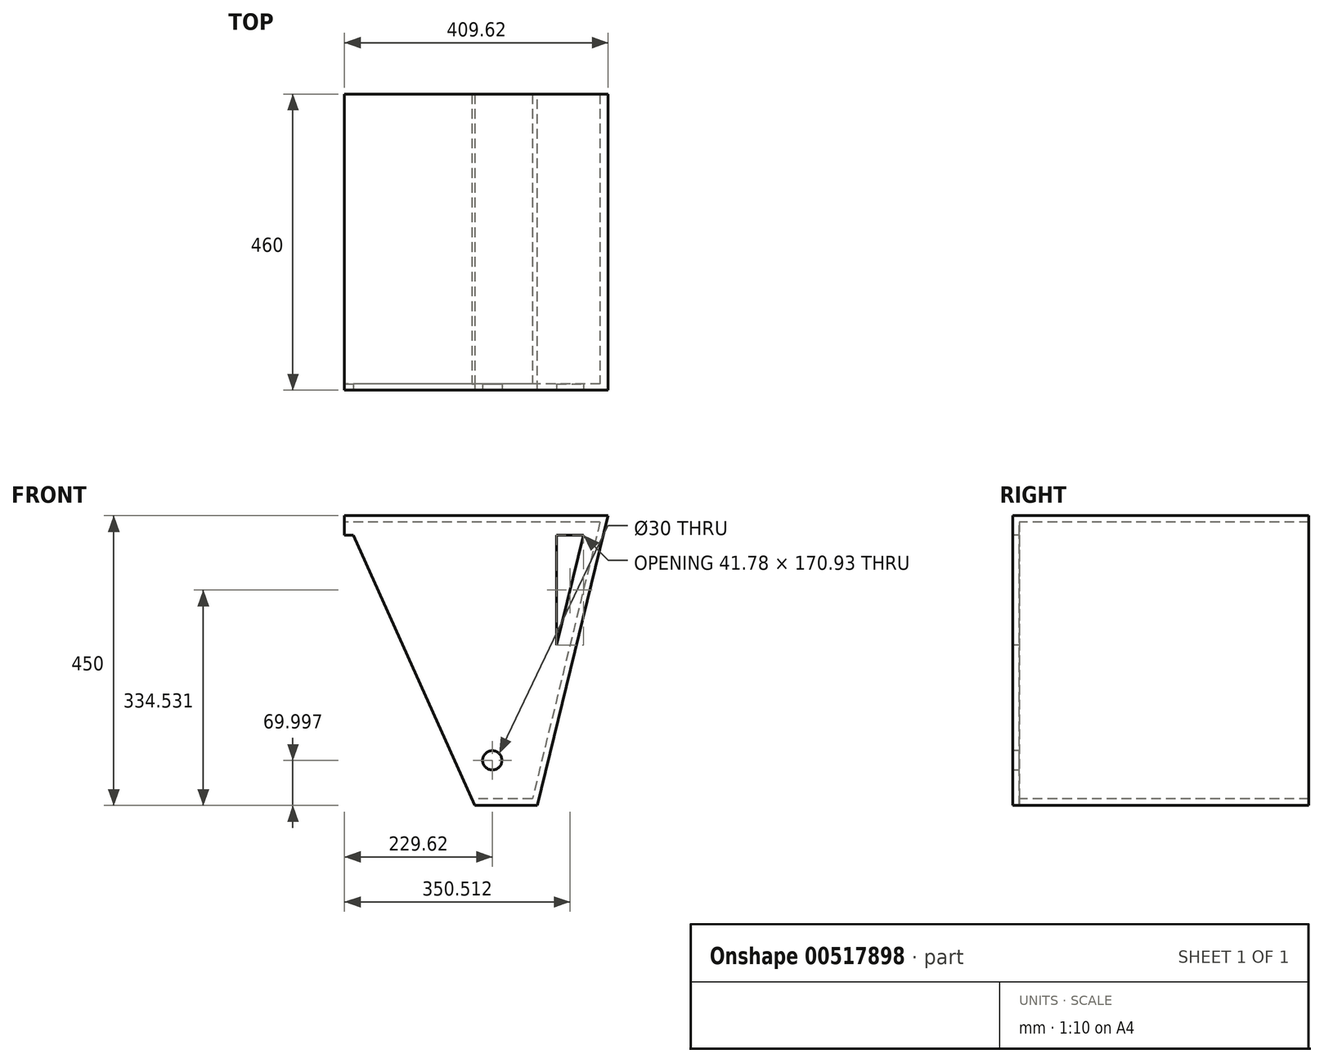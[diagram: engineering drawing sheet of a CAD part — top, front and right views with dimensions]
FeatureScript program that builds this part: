
annotation { "Feature Type Name" : "Feature", "Feature Type Description" : "" }
export const myFeature = defineFeature(function(context is Context, id is Id, definition is map)
    precondition{}
    {
        {
            var Q0;
            Q0=qCreatedBy(makeId("Front.planeOp"),FACE);
            var sketch = newSketch(context, id + "F0", { "sketchPlane" : qUnion([Q0])});
            skLineSegment(sketch, "E0.1", {"start": v(-436.34, 213.95) * mm, "end": v(-436.34, -176.05) * mm});
            skLineSegment(sketch, "E0.3", {"start": v(103.66, 213.95) * mm, "end": v(103.66, -176.05) * mm});
            skLineSegment(sketch, "E1", {"start": v(-465.58, -206.05) * mm, "end": v(133.66, -206.05) * mm});
            skLineSegment(sketch, "E2", {"start": v(-436.34, -176.05) * mm, "end": v(103.66, -176.05) * mm});
            skLineSegment(sketch, "E3", {"start": v(-436.34, 213.95) * mm, "end": v(103.66, 213.95) * mm});
            skLineSegment(sketch, "E4", {"start": v(-465.58, 243.95) * mm, "end": v(133.66, 243.95) * mm});
            skLineSegment(sketch, "E5", {"start": v(-465.58, 243.95) * mm, "end": v(-575.58, 243.95) * mm});
            skLineSegment(sketch, "E6", {"start": v(133.66, 243.95) * mm, "end": v(243.66, 243.95) * mm});
            skLineSegment(sketch, "E7", {"start": v(-575.58, 243.95) * mm, "end": v(-465.58, -206.05) * mm});
            skLineSegment(sketch, "E8", {"start": v(243.66, 243.95) * mm, "end": v(133.66, -206.05) * mm});
            skLineSegment(sketch, "E9.0", {"start": v(-537.36, 213.95) * mm, "end": v(-495.58, 43.02) * mm});
            skLineSegment(sketch, "E9.1", {"start": v(-495.58, 213.95) * mm, "end": v(-537.36, 213.95) * mm});
            skLineSegment(sketch, "E9.2", {"start": v(-495.58, 213.95) * mm, "end": v(-495.58, 43.02) * mm});
            skLineSegment(sketch, "E10.0", {"start": v(205.44, 213.95) * mm, "end": v(163.66, 43.02) * mm});
            skLineSegment(sketch, "E10.1", {"start": v(163.66, 213.95) * mm, "end": v(205.44, 213.95) * mm});
            skLineSegment(sketch, "E10.2", {"start": v(163.66, 213.95) * mm, "end": v(163.66, 43.02) * mm});
            skSolve(sketch);
        }
        {
            var Q0;
            Q0=makeQuery(id+"F0.imprint","IMPRINT",FACE,{"disambiguationData":[TD([[makeQuery(id+"F0.imprint","IMPRINT",EDGE,{"derivedFrom":sQuery(id+"F0.wireOp",EDGE,"E0.1")}),-1.0]])]});
            extrude(context, id + "F1", {"entities" : qUnion([Q0]), "depth" : 10 * mm, "offsetDistance" : 25 * mm});
        }
        {
            var Q0;
            Q0=makeQuery(id+"F1.opExtrude","CAP_FACE",FACE,{"disambiguationData":[OSD([sQuery(id+"F0.wireOp",EDGE,"E0.1"),sQuery(id+"F0.wireOp",EDGE,"E0.3"),sQuery(id+"F0.wireOp",EDGE,"E1"),sQuery(id+"F0.wireOp",EDGE,"E2"),sQuery(id+"F0.wireOp",EDGE,"E3"),sQuery(id+"F0.wireOp",EDGE,"E4"),sQuery(id+"F0.wireOp",EDGE,"E5"),sQuery(id+"F0.wireOp",EDGE,"E6"),sQuery(id+"F0.wireOp",EDGE,"E7"),sQuery(id+"F0.wireOp",EDGE,"E8"),sQuery(id+"F0.wireOp",EDGE,"E9.0"),sQuery(id+"F0.wireOp",EDGE,"E9.1"),sQuery(id+"F0.wireOp",EDGE,"E9.2"),sQuery(id+"F0.wireOp",EDGE,"E10.0"),sQuery(id+"F0.wireOp",EDGE,"E10.1"),sQuery(id+"F0.wireOp",EDGE,"E10.2")])],"isStart":false});
            var sketch = newSketch(context, id + "F2", { "sketchPlane" : qUnion([Q0])});
            skLineSegment(sketch, "E11.bottom", {"start": v(-436.34, 213.95) * mm, "end": v(-356.34, 213.95) * mm});
            skLineSegment(sketch, "E11.top", {"start": v(-436.34, 133.95) * mm, "end": v(-356.34, 133.95) * mm});
            skLineSegment(sketch, "E11.left", {"start": v(-436.34, 213.95) * mm, "end": v(-436.34, 133.95) * mm});
            skLineSegment(sketch, "E11.right", {"start": v(-356.34, 213.95) * mm, "end": v(-356.34, 133.95) * mm});
            skLineSegment(sketch, "E12.bottom", {"start": v(103.66, 213.95) * mm, "end": v(23.66, 213.95) * mm});
            skLineSegment(sketch, "E12.top", {"start": v(103.66, 133.95) * mm, "end": v(23.66, 133.95) * mm});
            skLineSegment(sketch, "E12.left", {"start": v(103.66, 213.95) * mm, "end": v(103.66, 133.95) * mm});
            skLineSegment(sketch, "E12.right", {"start": v(23.66, 213.95) * mm, "end": v(23.66, 133.95) * mm});
            skLineSegment(sketch, "E13.bottom", {"start": v(-436.34, -176.05) * mm, "end": v(-356.34, -176.05) * mm});
            skLineSegment(sketch, "E13.top", {"start": v(-436.34, -96.05) * mm, "end": v(-356.34, -96.05) * mm});
            skLineSegment(sketch, "E13.left", {"start": v(-436.34, -176.05) * mm, "end": v(-436.34, -96.05) * mm});
            skLineSegment(sketch, "E13.right", {"start": v(-356.34, -176.05) * mm, "end": v(-356.34, -96.05) * mm});
            skLineSegment(sketch, "E14.bottom", {"start": v(103.66, -176.05) * mm, "end": v(23.66, -176.05) * mm});
            skLineSegment(sketch, "E14.top", {"start": v(103.66, -96.05) * mm, "end": v(23.66, -96.05) * mm});
            skLineSegment(sketch, "E14.left", {"start": v(103.66, -176.05) * mm, "end": v(103.66, -96.05) * mm});
            skLineSegment(sketch, "E14.right", {"start": v(23.66, -176.05) * mm, "end": v(23.66, -96.05) * mm});
            skCircle(sketch, "E15", {"center": v(-396.34, -136.05) * mm, "radius": 15 * mm});
            skCircle(sketch, "E16", {"center": v(-396.34, 173.95) * mm, "radius": 15 * mm});
            skCircle(sketch, "E17", {"center": v(63.66, 173.95) * mm, "radius": 15 * mm});
            skCircle(sketch, "E18", {"center": v(63.66, -136.05) * mm, "radius": 15 * mm});
            skSolve(sketch);
        }
        {
            var Q0;
            Q0=makeQuery(id+"F2.imprint","IMPRINT",FACE,{"disambiguationData":[TD([[makeQuery(id+"F2.imprint","IMPRINT",EDGE,{"derivedFrom":sQuery(id+"F2.wireOp",EDGE,"E11.bottom")}),-1.0]])]});
            var Q1;
            Q1=makeQuery(id+"F2.imprint","IMPRINT",FACE,{"disambiguationData":[TD([[makeQuery(id+"F2.imprint","IMPRINT",EDGE,{"derivedFrom":sQuery(id+"F2.wireOp",EDGE,"E12.bottom")}),-1.0]])]});
            var Q2;
            Q2=makeQuery(id+"F2.imprint","IMPRINT",FACE,{"disambiguationData":[TD([[makeQuery(id+"F2.imprint","IMPRINT",EDGE,{"derivedFrom":sQuery(id+"F2.wireOp",EDGE,"E14.bottom")}),1.0]])]});
            var Q3;
            Q3=makeQuery(id+"F2.imprint","IMPRINT",FACE,{"disambiguationData":[TD([[makeQuery(id+"F2.imprint","IMPRINT",EDGE,{"derivedFrom":sQuery(id+"F2.wireOp",EDGE,"E13.bottom")}),1.0]])]});
            extrude(context, id + "F3", {"entities" : qUnion([Q0, Q1, Q2, Q3]), "operationType" : NewBodyOperationType.ADD, "oppositeDirection" : true, "depth" : 10 * mm, "offsetDistance" : 25 * mm});
        }
        {
            var Q0;
            Q0=makeQuery(id+"F3.boolean.opBoolean","MERGE",FACE,{"derivedFrom":[makeQuery(id+"F1.opExtrude","CAP_FACE",FACE,{"disambiguationData":[OSD([sQuery(id+"F0.wireOp",EDGE,"E0.1"),sQuery(id+"F0.wireOp",EDGE,"E0.3"),sQuery(id+"F0.wireOp",EDGE,"E1"),sQuery(id+"F0.wireOp",EDGE,"E2"),sQuery(id+"F0.wireOp",EDGE,"E3"),sQuery(id+"F0.wireOp",EDGE,"E4"),sQuery(id+"F0.wireOp",EDGE,"E5"),sQuery(id+"F0.wireOp",EDGE,"E6"),sQuery(id+"F0.wireOp",EDGE,"E7"),sQuery(id+"F0.wireOp",EDGE,"E8"),sQuery(id+"F0.wireOp",EDGE,"E9.0"),sQuery(id+"F0.wireOp",EDGE,"E9.1"),sQuery(id+"F0.wireOp",EDGE,"E9.2"),sQuery(id+"F0.wireOp",EDGE,"E10.0"),sQuery(id+"F0.wireOp",EDGE,"E10.1"),sQuery(id+"F0.wireOp",EDGE,"E10.2")])],"isStart":false}),makeQuery(id+"F3.opExtrude","CAP_FACE",FACE,{"disambiguationData":[OSD([sQuery(id+"F2.wireOp",EDGE,"E11.bottom"),sQuery(id+"F2.wireOp",EDGE,"E11.top"),sQuery(id+"F2.wireOp",EDGE,"E11.left"),sQuery(id+"F2.wireOp",EDGE,"E11.right"),sQuery(id+"F2.wireOp",EDGE,"E16")])],"isStart":true}),makeQuery(id+"F3.opExtrude","CAP_FACE",FACE,{"disambiguationData":[OSD([sQuery(id+"F2.wireOp",EDGE,"E12.bottom"),sQuery(id+"F2.wireOp",EDGE,"E12.top"),sQuery(id+"F2.wireOp",EDGE,"E12.left"),sQuery(id+"F2.wireOp",EDGE,"E12.right"),sQuery(id+"F2.wireOp",EDGE,"E17")])],"isStart":true}),makeQuery(id+"F3.opExtrude","CAP_FACE",FACE,{"disambiguationData":[OSD([sQuery(id+"F2.wireOp",EDGE,"E13.bottom"),sQuery(id+"F2.wireOp",EDGE,"E13.top"),sQuery(id+"F2.wireOp",EDGE,"E13.left"),sQuery(id+"F2.wireOp",EDGE,"E13.right"),sQuery(id+"F2.wireOp",EDGE,"E15")])],"isStart":true}),makeQuery(id+"F3.opExtrude","CAP_FACE",FACE,{"disambiguationData":[OSD([sQuery(id+"F2.wireOp",EDGE,"E14.bottom"),sQuery(id+"F2.wireOp",EDGE,"E14.top"),sQuery(id+"F2.wireOp",EDGE,"E14.left"),sQuery(id+"F2.wireOp",EDGE,"E14.right"),sQuery(id+"F2.wireOp",EDGE,"E18")])],"isStart":true})]});
            var sketch = newSketch(context, id + "F4", { "sketchPlane" : qUnion([Q0])});
            skLineSegment(sketch, "E19", {"start": v(-165.96, -206.05) * mm, "end": v(-165.96, 243.95) * mm});
            skLineSegment(sketch, "E20", {"start": v(-165.96, 243.95) * mm, "end": v(-669.64, 243.95) * mm});
            skLineSegment(sketch, "E21", {"start": v(-669.64, 243.95) * mm, "end": v(-669.64, -206.05) * mm});
            skLineSegment(sketch, "E22", {"start": v(-669.64, -206.05) * mm, "end": v(-165.96, -206.05) * mm});
            skSolve(sketch);
        }
        {
            var Q0;
            {var subQ2=sQuery(id+"F4.wireOp",EDGE,"E21");Q0=makeQuery(id+"F4.imprint","IMPRINT",FACE,{"disambiguationData":[TD([[makeQuery(id+"F4.imprint","IMPRINT",EDGE,{"derivedFrom":subQ2}),1.0]])]});}
            var Q1;
            {var subQ1=makeQuery(id+"F1.opExtrude","CAP_EDGE",EDGE,{"disambiguationData":[OSD([sQuery(id+"F0.wireOp",EDGE,"E7")])],"isStart":false});Q1=makeQuery(id+"F4.imprint","IMPRINT",FACE,{"disambiguationData":[TD([[makeQuery(id+"F4.imprint","IMPRINT",EDGE,{"derivedFrom":subQ1}),1.0]])]});}
            var Q2;
            Q2=makeQuery(id+"F4.imprint","IMPRINT",FACE,{"disambiguationData":[TD([[makeQuery(id+"F4.imprint","IMPRINT",EDGE,{"derivedFrom":makeQuery(id+"F3.opExtrude","CAP_EDGE",EDGE,{"disambiguationData":[OSD([sQuery(id+"F2.wireOp",EDGE,"E11.top")])],"isStart":true})}),-1.0]])]});
            extrude(context, id + "F5", {"entities" : qUnion([Q0, Q1, Q2]), "operationType" : NewBodyOperationType.REMOVE, "oppositeDirection" : true, "depth" : 25 * mm, "offsetDistance" : 25 * mm});
        }
        {
            var Q0;
            Q0=makeQuery(id+"F3.boolean.opBoolean","MERGE",FACE,{"derivedFrom":[makeQuery(id+"F1.opExtrude","CAP_FACE",FACE,{"disambiguationData":[OSD([sQuery(id+"F0.wireOp",EDGE,"E0.1"),sQuery(id+"F0.wireOp",EDGE,"E0.3"),sQuery(id+"F0.wireOp",EDGE,"E1"),sQuery(id+"F0.wireOp",EDGE,"E2"),sQuery(id+"F0.wireOp",EDGE,"E3"),sQuery(id+"F0.wireOp",EDGE,"E4"),sQuery(id+"F0.wireOp",EDGE,"E5"),sQuery(id+"F0.wireOp",EDGE,"E6"),sQuery(id+"F0.wireOp",EDGE,"E7"),sQuery(id+"F0.wireOp",EDGE,"E8"),sQuery(id+"F0.wireOp",EDGE,"E9.0"),sQuery(id+"F0.wireOp",EDGE,"E9.1"),sQuery(id+"F0.wireOp",EDGE,"E9.2"),sQuery(id+"F0.wireOp",EDGE,"E10.0"),sQuery(id+"F0.wireOp",EDGE,"E10.1"),sQuery(id+"F0.wireOp",EDGE,"E10.2")])],"isStart":false}),makeQuery(id+"F3.opExtrude","CAP_FACE",FACE,{"disambiguationData":[OSD([sQuery(id+"F2.wireOp",EDGE,"E11.bottom"),sQuery(id+"F2.wireOp",EDGE,"E11.top"),sQuery(id+"F2.wireOp",EDGE,"E11.left"),sQuery(id+"F2.wireOp",EDGE,"E11.right"),sQuery(id+"F2.wireOp",EDGE,"E16")])],"isStart":true}),makeQuery(id+"F3.opExtrude","CAP_FACE",FACE,{"disambiguationData":[OSD([sQuery(id+"F2.wireOp",EDGE,"E12.bottom"),sQuery(id+"F2.wireOp",EDGE,"E12.top"),sQuery(id+"F2.wireOp",EDGE,"E12.left"),sQuery(id+"F2.wireOp",EDGE,"E12.right"),sQuery(id+"F2.wireOp",EDGE,"E17")])],"isStart":true}),makeQuery(id+"F3.opExtrude","CAP_FACE",FACE,{"disambiguationData":[OSD([sQuery(id+"F2.wireOp",EDGE,"E13.bottom"),sQuery(id+"F2.wireOp",EDGE,"E13.top"),sQuery(id+"F2.wireOp",EDGE,"E13.left"),sQuery(id+"F2.wireOp",EDGE,"E13.right"),sQuery(id+"F2.wireOp",EDGE,"E15")])],"isStart":true}),makeQuery(id+"F3.opExtrude","CAP_FACE",FACE,{"disambiguationData":[OSD([sQuery(id+"F2.wireOp",EDGE,"E14.bottom"),sQuery(id+"F2.wireOp",EDGE,"E14.top"),sQuery(id+"F2.wireOp",EDGE,"E14.left"),sQuery(id+"F2.wireOp",EDGE,"E14.right"),sQuery(id+"F2.wireOp",EDGE,"E18")])],"isStart":true})]});
            var sketch = newSketch(context, id + "F6", { "sketchPlane" : qUnion([Q0])});
            skLineSegment(sketch, "E23", {"start": v(23.66, -176.05) * mm, "end": v(36.2, -206.05) * mm});
            skLineSegment(sketch, "E24", {"start": v(36.2, -206.05) * mm, "end": v(-165.96, -206.05) * mm});
            skLineSegment(sketch, "E25", {"start": v(-165.96, -206.05) * mm, "end": v(-165.96, -176.05) * mm});
            skLineSegment(sketch, "E26", {"start": v(-165.96, -176.05) * mm, "end": v(23.66, -176.05) * mm});
            skSolve(sketch);
        }
        {
            var Q0;
            Q0=makeQuery(id+"F6.imprint","IMPRINT",FACE,{"disambiguationData":[TD([[makeQuery(id+"F6.imprint","IMPRINT",EDGE,{"derivedFrom":sQuery(id+"F6.wireOp",EDGE,"E23")}),-1.0]])]});
            extrude(context, id + "F7", {"entities" : qUnion([Q0]), "operationType" : NewBodyOperationType.REMOVE, "oppositeDirection" : true, "depth" : 25 * mm, "offsetDistance" : 25 * mm});
        }
        {
            var Q0;
            Q0=makeQuery(id+"F3.boolean.opBoolean","MERGE",FACE,{"derivedFrom":[makeQuery(id+"F1.opExtrude","CAP_FACE",FACE,{"disambiguationData":[OSD([sQuery(id+"F0.wireOp",EDGE,"E0.1"),sQuery(id+"F0.wireOp",EDGE,"E0.3"),sQuery(id+"F0.wireOp",EDGE,"E1"),sQuery(id+"F0.wireOp",EDGE,"E2"),sQuery(id+"F0.wireOp",EDGE,"E3"),sQuery(id+"F0.wireOp",EDGE,"E4"),sQuery(id+"F0.wireOp",EDGE,"E5"),sQuery(id+"F0.wireOp",EDGE,"E6"),sQuery(id+"F0.wireOp",EDGE,"E7"),sQuery(id+"F0.wireOp",EDGE,"E8"),sQuery(id+"F0.wireOp",EDGE,"E9.0"),sQuery(id+"F0.wireOp",EDGE,"E9.1"),sQuery(id+"F0.wireOp",EDGE,"E9.2"),sQuery(id+"F0.wireOp",EDGE,"E10.0"),sQuery(id+"F0.wireOp",EDGE,"E10.1"),sQuery(id+"F0.wireOp",EDGE,"E10.2")])],"isStart":false}),makeQuery(id+"F3.opExtrude","CAP_FACE",FACE,{"disambiguationData":[OSD([sQuery(id+"F2.wireOp",EDGE,"E11.bottom"),sQuery(id+"F2.wireOp",EDGE,"E11.top"),sQuery(id+"F2.wireOp",EDGE,"E11.left"),sQuery(id+"F2.wireOp",EDGE,"E11.right"),sQuery(id+"F2.wireOp",EDGE,"E16")])],"isStart":true}),makeQuery(id+"F3.opExtrude","CAP_FACE",FACE,{"disambiguationData":[OSD([sQuery(id+"F2.wireOp",EDGE,"E12.bottom"),sQuery(id+"F2.wireOp",EDGE,"E12.top"),sQuery(id+"F2.wireOp",EDGE,"E12.left"),sQuery(id+"F2.wireOp",EDGE,"E12.right"),sQuery(id+"F2.wireOp",EDGE,"E17")])],"isStart":true}),makeQuery(id+"F3.opExtrude","CAP_FACE",FACE,{"disambiguationData":[OSD([sQuery(id+"F2.wireOp",EDGE,"E13.bottom"),sQuery(id+"F2.wireOp",EDGE,"E13.top"),sQuery(id+"F2.wireOp",EDGE,"E13.left"),sQuery(id+"F2.wireOp",EDGE,"E13.right"),sQuery(id+"F2.wireOp",EDGE,"E15")])],"isStart":true}),makeQuery(id+"F3.opExtrude","CAP_FACE",FACE,{"disambiguationData":[OSD([sQuery(id+"F2.wireOp",EDGE,"E14.bottom"),sQuery(id+"F2.wireOp",EDGE,"E14.top"),sQuery(id+"F2.wireOp",EDGE,"E14.left"),sQuery(id+"F2.wireOp",EDGE,"E14.right"),sQuery(id+"F2.wireOp",EDGE,"E18")])],"isStart":true})]});
            var sketch = newSketch(context, id + "F8", { "sketchPlane" : qUnion([Q0])});
            skLineSegment(sketch, "E27", {"start": v(23.66, 213.95) * mm, "end": v(114.09, 213.95) * mm});
            skLineSegment(sketch, "E28", {"start": v(103.66, 133.95) * mm, "end": v(103.66, 230.37) * mm});
            skSolve(sketch);
        }
        {
            var Q0;
            {var subQ1=makeQuery(id+"F3.opExtrude","CAP_EDGE",EDGE,{"disambiguationData":[OSD([sQuery(id+"F2.wireOp",EDGE,"E12.top")])],"isStart":true});Q0=makeQuery(id+"F8.imprint","IMPRINT",FACE,{"disambiguationData":[TD([[makeQuery(id+"F8.imprint","IMPRINT",EDGE,{"derivedFrom":subQ1}),-1.0]])]});}
            extrude(context, id + "F9", {"entities" : qUnion([Q0]), "operationType" : NewBodyOperationType.REMOVE, "oppositeDirection" : true, "depth" : 25 * mm, "offsetDistance" : 25 * mm});
        }
        {
            var Q0;
            Q0=makeQuery(id+"F3.boolean.opBoolean","MERGE",FACE,{"derivedFrom":[makeQuery(id+"F1.opExtrude","CAP_FACE",FACE,{"disambiguationData":[OSD([sQuery(id+"F0.wireOp",EDGE,"E0.1"),sQuery(id+"F0.wireOp",EDGE,"E0.3"),sQuery(id+"F0.wireOp",EDGE,"E1"),sQuery(id+"F0.wireOp",EDGE,"E2"),sQuery(id+"F0.wireOp",EDGE,"E3"),sQuery(id+"F0.wireOp",EDGE,"E4"),sQuery(id+"F0.wireOp",EDGE,"E5"),sQuery(id+"F0.wireOp",EDGE,"E6"),sQuery(id+"F0.wireOp",EDGE,"E7"),sQuery(id+"F0.wireOp",EDGE,"E8"),sQuery(id+"F0.wireOp",EDGE,"E9.0"),sQuery(id+"F0.wireOp",EDGE,"E9.1"),sQuery(id+"F0.wireOp",EDGE,"E9.2"),sQuery(id+"F0.wireOp",EDGE,"E10.0"),sQuery(id+"F0.wireOp",EDGE,"E10.1"),sQuery(id+"F0.wireOp",EDGE,"E10.2")])],"isStart":false}),makeQuery(id+"F3.opExtrude","CAP_FACE",FACE,{"disambiguationData":[OSD([sQuery(id+"F2.wireOp",EDGE,"E11.bottom"),sQuery(id+"F2.wireOp",EDGE,"E11.top"),sQuery(id+"F2.wireOp",EDGE,"E11.left"),sQuery(id+"F2.wireOp",EDGE,"E11.right"),sQuery(id+"F2.wireOp",EDGE,"E16")])],"isStart":true}),makeQuery(id+"F3.opExtrude","CAP_FACE",FACE,{"disambiguationData":[OSD([sQuery(id+"F2.wireOp",EDGE,"E12.bottom"),sQuery(id+"F2.wireOp",EDGE,"E12.top"),sQuery(id+"F2.wireOp",EDGE,"E12.left"),sQuery(id+"F2.wireOp",EDGE,"E12.right"),sQuery(id+"F2.wireOp",EDGE,"E17")])],"isStart":true}),makeQuery(id+"F3.opExtrude","CAP_FACE",FACE,{"disambiguationData":[OSD([sQuery(id+"F2.wireOp",EDGE,"E13.bottom"),sQuery(id+"F2.wireOp",EDGE,"E13.top"),sQuery(id+"F2.wireOp",EDGE,"E13.left"),sQuery(id+"F2.wireOp",EDGE,"E13.right"),sQuery(id+"F2.wireOp",EDGE,"E15")])],"isStart":true}),makeQuery(id+"F3.opExtrude","CAP_FACE",FACE,{"disambiguationData":[OSD([sQuery(id+"F2.wireOp",EDGE,"E14.bottom"),sQuery(id+"F2.wireOp",EDGE,"E14.top"),sQuery(id+"F2.wireOp",EDGE,"E14.left"),sQuery(id+"F2.wireOp",EDGE,"E14.right"),sQuery(id+"F2.wireOp",EDGE,"E18")])],"isStart":true})]});
            var sketch = newSketch(context, id + "F10", { "sketchPlane" : qUnion([Q0])});
            skLineSegment(sketch, "E29", {"start": v(163.66, 213.95) * mm, "end": v(205.44, 213.95) * mm});
            skLineSegment(sketch, "E30", {"start": v(205.44, 213.95) * mm, "end": v(163.66, 43.02) * mm});
            skLineSegment(sketch, "E31", {"start": v(163.66, 43.02) * mm, "end": v(163.66, 213.95) * mm});
            skSolve(sketch);
        }
        {
            var Q0;
            Q0=makeQuery(id+"F10.imprint","IMPRINT",FACE,{"disambiguationData":[TD([[makeQuery(id+"F10.imprint","IMPRINT",EDGE,{"derivedFrom":sQuery(id+"F10.wireOp",EDGE,"E29")}),-1.0]])]});
            extrude(context, id + "F11", {"entities" : qUnion([Q0]), "oppositeDirection" : true, "depth" : 10 * mm, "offsetDistance" : 25 * mm});
        }
        {
            var Q0;
            Q0=makeQuery(id+"F3.boolean.opBoolean","MERGE",FACE,{"derivedFrom":[makeQuery(id+"F1.opExtrude","CAP_FACE",FACE,{"disambiguationData":[OSD([sQuery(id+"F0.wireOp",EDGE,"E0.1"),sQuery(id+"F0.wireOp",EDGE,"E0.3"),sQuery(id+"F0.wireOp",EDGE,"E1"),sQuery(id+"F0.wireOp",EDGE,"E2"),sQuery(id+"F0.wireOp",EDGE,"E3"),sQuery(id+"F0.wireOp",EDGE,"E4"),sQuery(id+"F0.wireOp",EDGE,"E5"),sQuery(id+"F0.wireOp",EDGE,"E6"),sQuery(id+"F0.wireOp",EDGE,"E7"),sQuery(id+"F0.wireOp",EDGE,"E8"),sQuery(id+"F0.wireOp",EDGE,"E9.0"),sQuery(id+"F0.wireOp",EDGE,"E9.1"),sQuery(id+"F0.wireOp",EDGE,"E9.2"),sQuery(id+"F0.wireOp",EDGE,"E10.0"),sQuery(id+"F0.wireOp",EDGE,"E10.1"),sQuery(id+"F0.wireOp",EDGE,"E10.2")])],"isStart":true}),makeQuery(id+"F3.opExtrude","CAP_FACE",FACE,{"disambiguationData":[OSD([sQuery(id+"F2.wireOp",EDGE,"E11.bottom"),sQuery(id+"F2.wireOp",EDGE,"E11.top"),sQuery(id+"F2.wireOp",EDGE,"E11.left"),sQuery(id+"F2.wireOp",EDGE,"E11.right"),sQuery(id+"F2.wireOp",EDGE,"E16")])],"isStart":false}),makeQuery(id+"F3.opExtrude","CAP_FACE",FACE,{"disambiguationData":[OSD([sQuery(id+"F2.wireOp",EDGE,"E12.bottom"),sQuery(id+"F2.wireOp",EDGE,"E12.top"),sQuery(id+"F2.wireOp",EDGE,"E12.left"),sQuery(id+"F2.wireOp",EDGE,"E12.right"),sQuery(id+"F2.wireOp",EDGE,"E17")])],"isStart":false}),makeQuery(id+"F3.opExtrude","CAP_FACE",FACE,{"disambiguationData":[OSD([sQuery(id+"F2.wireOp",EDGE,"E13.bottom"),sQuery(id+"F2.wireOp",EDGE,"E13.top"),sQuery(id+"F2.wireOp",EDGE,"E13.left"),sQuery(id+"F2.wireOp",EDGE,"E13.right"),sQuery(id+"F2.wireOp",EDGE,"E15")])],"isStart":false}),makeQuery(id+"F3.opExtrude","CAP_FACE",FACE,{"disambiguationData":[OSD([sQuery(id+"F2.wireOp",EDGE,"E14.bottom"),sQuery(id+"F2.wireOp",EDGE,"E14.top"),sQuery(id+"F2.wireOp",EDGE,"E14.left"),sQuery(id+"F2.wireOp",EDGE,"E14.right"),sQuery(id+"F2.wireOp",EDGE,"E18")])],"isStart":false})]});
            var sketch = newSketch(context, id + "F12", { "sketchPlane" : qUnion([Q0])});
            skLineSegment(sketch, "E32", {"start": v(-243.66, 243.95) * mm, "end": v(-133.66, -206.05) * mm});
            skLineSegment(sketch, "E33", {"start": v(-133.66, -206.05) * mm, "end": v(-36.2, -206.05) * mm});
            skLineSegment(sketch, "E34", {"start": v(-243.66, 243.95) * mm, "end": v(165.96, 243.95) * mm});
            skLineSegment(sketch, "E35.0", {"start": v(-230.92, 233.95) * mm, "end": v(165.96, 233.95) * mm});
            skLineSegment(sketch, "E35.1", {"start": v(-230.92, 233.95) * mm, "end": v(-125.81, -196.05) * mm});
            skLineSegment(sketch, "E35.2", {"start": v(-125.81, -196.05) * mm, "end": v(-36.2, -196.05) * mm});
            skLineSegment(sketch, "E36", {"start": v(-36.2, -206.05) * mm, "end": v(-23.66, -176.05) * mm});
            skLineSegment(sketch, "E37", {"start": v(-36.2, -196.05) * mm, "end": v(15.32, -196.05) * mm});
            skLineSegment(sketch, "E38", {"start": v(165.96, 233.95) * mm, "end": v(165.96, 243.95) * mm});
            skSolve(sketch);
        }
        {
            var Q0;
            Q0=makeQuery(id+"F12.imprint","IMPRINT",FACE,{"disambiguationData":[TD([[makeQuery(id+"F12.imprint","IMPRINT",EDGE,{"derivedFrom":sQuery(id+"F12.wireOp",EDGE,"E32")}),1.0]])]});
            extrude(context, id + "F13", {"entities" : qUnion([Q0]), "operationType" : NewBodyOperationType.ADD, "depth" : 450 * mm, "offsetDistance" : 25 * mm});
        }
        {
            var Q0;
            Q0=makeQuery(id+"F3.boolean.opBoolean","MERGE",FACE,{"derivedFrom":[makeQuery(id+"F1.opExtrude","CAP_FACE",FACE,{"disambiguationData":[OSD([sQuery(id+"F0.wireOp",EDGE,"E0.1"),sQuery(id+"F0.wireOp",EDGE,"E0.3"),sQuery(id+"F0.wireOp",EDGE,"E1"),sQuery(id+"F0.wireOp",EDGE,"E2"),sQuery(id+"F0.wireOp",EDGE,"E3"),sQuery(id+"F0.wireOp",EDGE,"E4"),sQuery(id+"F0.wireOp",EDGE,"E5"),sQuery(id+"F0.wireOp",EDGE,"E6"),sQuery(id+"F0.wireOp",EDGE,"E7"),sQuery(id+"F0.wireOp",EDGE,"E8"),sQuery(id+"F0.wireOp",EDGE,"E9.0"),sQuery(id+"F0.wireOp",EDGE,"E9.1"),sQuery(id+"F0.wireOp",EDGE,"E9.2"),sQuery(id+"F0.wireOp",EDGE,"E10.0"),sQuery(id+"F0.wireOp",EDGE,"E10.1"),sQuery(id+"F0.wireOp",EDGE,"E10.2")])],"isStart":false}),makeQuery(id+"F3.opExtrude","CAP_FACE",FACE,{"disambiguationData":[OSD([sQuery(id+"F2.wireOp",EDGE,"E11.bottom"),sQuery(id+"F2.wireOp",EDGE,"E11.top"),sQuery(id+"F2.wireOp",EDGE,"E11.left"),sQuery(id+"F2.wireOp",EDGE,"E11.right"),sQuery(id+"F2.wireOp",EDGE,"E16")])],"isStart":true}),makeQuery(id+"F3.opExtrude","CAP_FACE",FACE,{"disambiguationData":[OSD([sQuery(id+"F2.wireOp",EDGE,"E12.bottom"),sQuery(id+"F2.wireOp",EDGE,"E12.top"),sQuery(id+"F2.wireOp",EDGE,"E12.left"),sQuery(id+"F2.wireOp",EDGE,"E12.right"),sQuery(id+"F2.wireOp",EDGE,"E17")])],"isStart":true}),makeQuery(id+"F3.opExtrude","CAP_FACE",FACE,{"disambiguationData":[OSD([sQuery(id+"F2.wireOp",EDGE,"E13.bottom"),sQuery(id+"F2.wireOp",EDGE,"E13.top"),sQuery(id+"F2.wireOp",EDGE,"E13.left"),sQuery(id+"F2.wireOp",EDGE,"E13.right"),sQuery(id+"F2.wireOp",EDGE,"E15")])],"isStart":true}),makeQuery(id+"F3.opExtrude","CAP_FACE",FACE,{"disambiguationData":[OSD([sQuery(id+"F2.wireOp",EDGE,"E14.bottom"),sQuery(id+"F2.wireOp",EDGE,"E14.top"),sQuery(id+"F2.wireOp",EDGE,"E14.left"),sQuery(id+"F2.wireOp",EDGE,"E14.right"),sQuery(id+"F2.wireOp",EDGE,"E18")])],"isStart":true})]});
            var sketch = newSketch(context, id + "F14", { "sketchPlane" : qUnion([Q0])});
            skLineSegment(sketch, "E39", {"start": v(36.2, -206.05) * mm, "end": v(-152.26, 213.95) * mm});
            skSolve(sketch);
        }
        {
            var Q0;
            {var subQ0=sQuery(id+"F14.wireOp",EDGE,"E39");Q0=makeQuery(id+"F14.imprint","IMPRINT",FACE,{"disambiguationData":[TD([[makeQuery(id+"F14.imprint","IMPRINT",EDGE,{"derivedFrom":subQ0}),-1.0]])]});}
            extrude(context, id + "F15", {"entities" : qUnion([Q0]), "operationType" : NewBodyOperationType.ADD, "oppositeDirection" : true, "depth" : 10 * mm, "offsetDistance" : 25 * mm});
        }
    });
